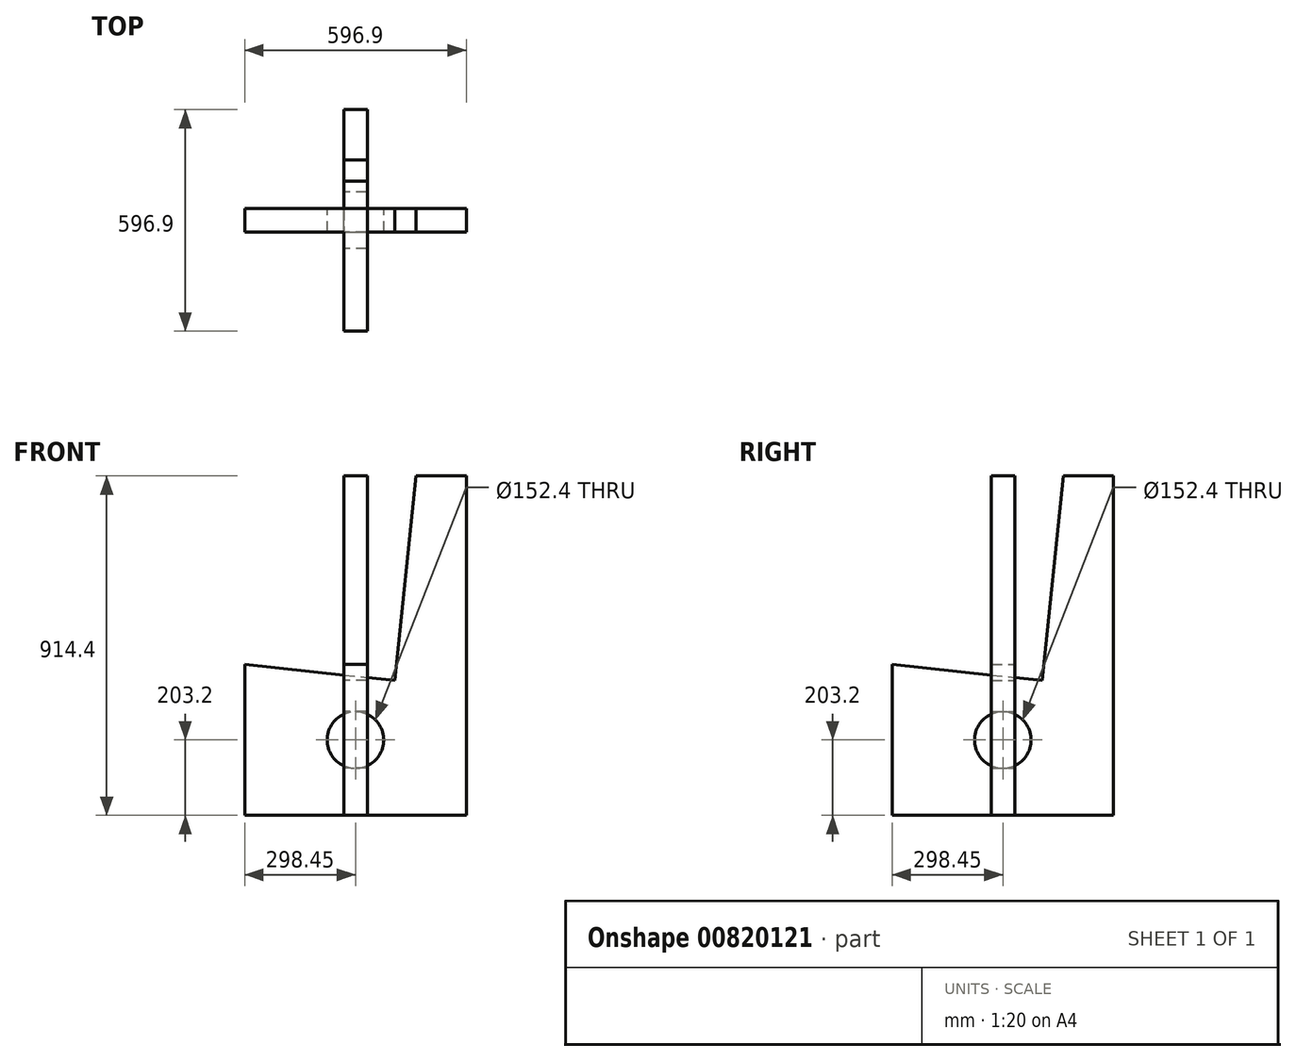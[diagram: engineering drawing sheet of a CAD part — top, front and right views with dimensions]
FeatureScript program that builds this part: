
annotation { "Feature Type Name" : "Feature", "Feature Type Description" : "" }
export const myFeature = defineFeature(function(context is Context, id is Id, definition is map)
    precondition{}
    {
        {
            var Q0;
            Q0=qCreatedBy(makeId("Front.planeOp"),FACE);
            var sketch = newSketch(context, id + "F0", { "sketchPlane" : qUnion([Q0])});
            skLineSegment(sketch, "E0.bottom", {"start": v(0, 0) * mm, "end": v(596.9, 0) * mm});
            skLineSegment(sketch, "E0.top", {"start": v(462.03, 914.4) * mm, "end": v(596.9, 914.4) * mm});
            skLineSegment(sketch, "E0.left", {"start": v(0, 0) * mm, "end": v(0, 406.4) * mm});
            skLineSegment(sketch, "E0.right", {"start": v(596.9, 0) * mm, "end": v(596.9, 914.4) * mm});
            skLineSegment(sketch, "E1", {"start": v(0, 406.4) * mm, "end": v(404.17, 363.92) * mm});
            skLineSegment(sketch, "E2", {"start": v(404.17, 363.92) * mm, "end": v(462.03, 914.4) * mm});
            skLineSegment(sketch, "E3", {"start": v(596.9, 0) * mm, "end": v(596.9, 203.2) * mm});
            skLineSegment(sketch, "E4", {"start": v(298.45, 203.2) * mm, "end": v(298.45, 0) * mm});
            skCircle(sketch, "E5", {"center": v(298.45, 203.2) * mm, "radius": 76.2 * mm});
            skLineSegment(sketch, "E6", {"start": v(298.45, 0) * mm, "end": v(298.45, 127) * mm});
            skSolve(sketch);
        }
        {
            var Q0;
            Q0 = qSketchRegion(id + "F0", true);
            extrude(context, id + "F1", {"entities" : qUnion([Q0]), "depth" : 63.5 * mm, "offsetDistance" : 25 * mm});
        }
        {
            var Q0;
            Q0=makeQuery(id+"F1.opExtrude","SWEPT_BODY",BODY,{"disambiguationData":[OSD([sQuery(id+"F0.wireOp",EDGE,"E0.bottom"),sQuery(id+"F0.wireOp",EDGE,"E0.top"),sQuery(id+"F0.wireOp",EDGE,"E0.right"),sQuery(id+"F0.wireOp",EDGE,"E0.left"),sQuery(id+"F0.wireOp",EDGE,"E1"),sQuery(id+"F0.wireOp",EDGE,"E2"),sQuery(id+"F0.wireOp",EDGE,"E3"),sQuery(id+"F0.wireOp",EDGE,"E5")])]});
            transform(context, id + "F2", {"entities" : qUnion([Q0]), "transformType" : TransformType.COPY});
        }
        {
            var Q0;
            Q0=makeQuery(id+"F1.opExtrude","SWEPT_FACE",FACE,{"disambiguationData":[OSD([sQuery(id+"F0.wireOp",EDGE,"E0.bottom")])]});
            var sketch = newSketch(context, id + "F3", { "sketchPlane" : qUnion([Q0])});
            skLineSegment(sketch, "E7", {"start": v(298.45, 0) * mm, "end": v(298.45, 63.5) * mm});
            skLineSegment(sketch, "E8", {"start": v(298.45, 63.5) * mm, "end": v(298.45, 31.75) * mm});
            skCircle(sketch, "E9", {"center": v(298.45, 31.75) * mm, "radius": 31.75 * mm});
            skSolve(sketch);
        }
        {
            var Q0;
            {var subQ0=sQuery(id+"F3.wireOp",EDGE,"E7");Q0=makeQuery(id+"F3.imprint","IMPRINT",FACE,{"disambiguationData":[TD([[makeQuery(id+"F3.imprint","IMPRINT",EDGE,{"derivedFrom":subQ0}),-1.0]])]});}
            extrude(context, id + "F4", {"entities" : qUnion([Q0]), "oppositeDirection" : true, "depth" : 609.6 * mm, "offsetDistance" : 25 * mm});
        }
        {
            var Q0;
            Q0=makeQuery(id+"F4.opExtrude","SWEPT_FACE",FACE,{"disambiguationData":[OSD([sQuery(id+"F3.wireOp",EDGE,"E7"),sQuery(id+"F3.wireOp",EDGE,"E8")])]});
            var sketch = newSketch(context, id + "F5", { "sketchPlane" : qUnion([Q0])});
            skLineSegment(sketch, "E10", {"start": v(31.75, 0) * mm, "end": v(31.75, 609.6) * mm});
            skSolve(sketch);
        }
        {
            var Q0;
            Q0=makeQuery(id+"F1.opExtrude","SWEPT_BODY",BODY,{"disambiguationData":[OSD([sQuery(id+"F0.wireOp",EDGE,"E0.bottom"),sQuery(id+"F0.wireOp",EDGE,"E0.top"),sQuery(id+"F0.wireOp",EDGE,"E0.right"),sQuery(id+"F0.wireOp",EDGE,"E0.left"),sQuery(id+"F0.wireOp",EDGE,"E1"),sQuery(id+"F0.wireOp",EDGE,"E2"),sQuery(id+"F0.wireOp",EDGE,"E3"),sQuery(id+"F0.wireOp",EDGE,"E5")])]});
            var Q1;
            Q1=sQuery(id+"F5.wireOp",EDGE,"E10");
            transform(context, id + "F6", {"entities" : qUnion([Q0]), "transformType" : TransformType.ROTATION, "transformAxis" : qUnion([Q1]), "angle" : 90 * degree, "makeCopy" : false});
        }
        {
            var Q0;
            Q0=makeQuery(id+"F4.opExtrude","SWEPT_BODY",BODY,{"disambiguationData":[OSD([sQuery(id+"F3.wireOp",EDGE,"E7"),sQuery(id+"F3.wireOp",EDGE,"E8"),sQuery(id+"F3.wireOp",EDGE,"E9")])]});
            deleteBodies(context, id + "F7", {"entities" : qUnion([Q0])});
        }
    });
